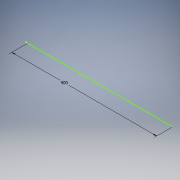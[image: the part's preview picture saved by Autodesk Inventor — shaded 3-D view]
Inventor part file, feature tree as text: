
AUTODESK INVENTOR PART (.ipt)
format: ipt  version: 2018 (Build 220112000, 112)  size: 83,968 bytes
history: native  units: mm
features: sketch x1
ambient origin geometry x8: Origin, YZ Plane, XZ Plane, XY Plane, X Axis, Y Axis, Z Axis, Center Point
feature tree (1):
  sketch  "Sketch1"  dims[d0=900.0mm]
